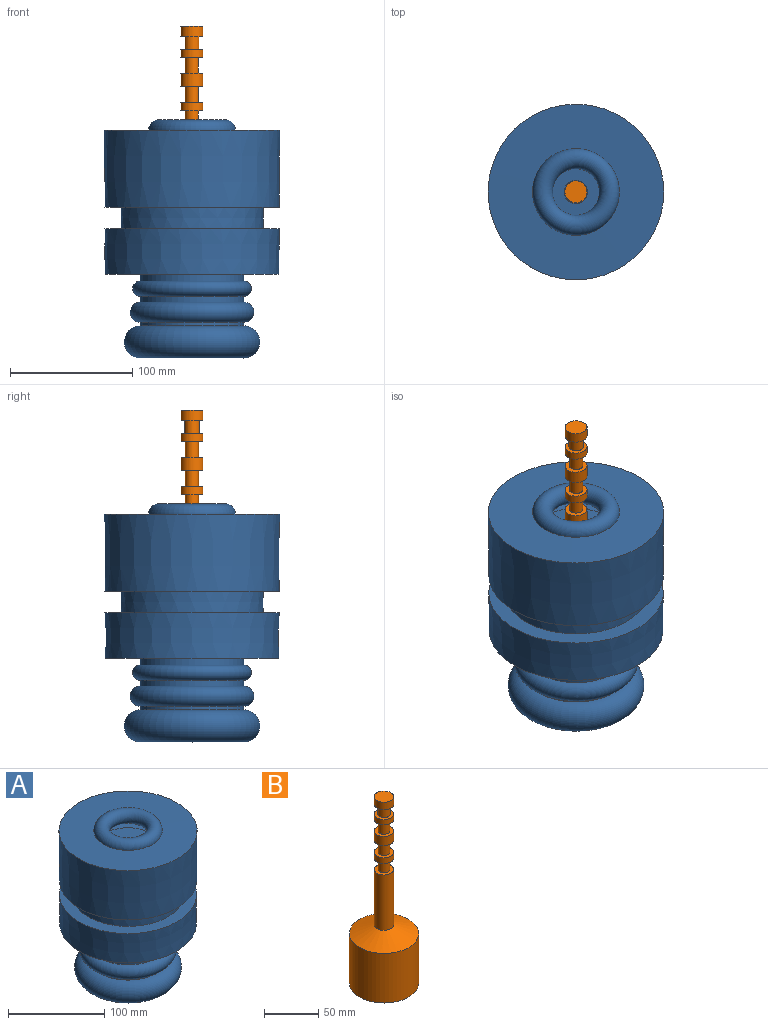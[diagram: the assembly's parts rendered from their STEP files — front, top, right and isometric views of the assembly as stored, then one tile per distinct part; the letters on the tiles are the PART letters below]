
ASSEMBLY  parts=2 mates=1
PART A: 47 faces, bbox 143.7x143.7x194.9 mm
  f0: torus R=42.43mm, axis (0,0,1), area 7727.4mm2, adj f1,f46
  f1: cylinder r=42.43mm len=84.86mm, axis (0,0,1), area 785.9mm2, adj f0,f2
  f2: torus R=42.43mm, axis (0,0,1), area 17605.2mm2, adj f1,f3
  f3: plane 58.56x58.56mm, normal (0,0,-1), area 2693.2mm2, adj f2
  f4: plane 42.43x42.43mm, normal (0,0,1), area 1413.9mm2, adj f5
  f5: cone r=21.7mm half-angle=19.1deg, axis (0,0,-1), area 198.9mm2, adj f4,f6
  f6: plane 47.27x47.27mm, normal (0,0,1), area 275.7mm2, adj f5,f7
  f7: cylinder r=23.63mm len=47.27mm, axis (0,0,1), area 293mm2, adj f6,f8
  f8: plane 47.27x47.27mm, normal (0,0,-1), area 181.2mm2, adj f7,f9
  f9: cone r=24.95mm half-angle=19.1deg, axis (0,0,-1), area 1168.6mm2, adj f8,f10
  f10: plane 53.77x53.77mm, normal (0,0,1), area 315.3mm2, adj f9,f11
  f11: cylinder r=26.88mm len=53.77mm, axis (0,0,1), area 333.3mm2, adj f10,f12
  f12: plane 53.77x53.77mm, normal (0,0,-1), area 206.8mm2, adj f11,f13
  f13: cone r=28.2mm half-angle=19.1deg, axis (0,0,-1), area 1329.2mm2, adj f12,f14
  f14: plane 60.27x60.27mm, normal (0,0,1), area 354.8mm2, adj f13,f15
  f15: cylinder r=30.14mm len=60.27mm, axis (0,0,1), area 373.6mm2, adj f14,f16
  f16: plane 60.27x60.27mm, normal (0,0,-1), area 232.4mm2, adj f15,f17
  f17: cone r=31.45mm half-angle=19.1deg, axis (0,0,-1), area 1489.8mm2, adj f16,f18
  f18: plane 66.78x66.78mm, normal (0,0,1), area 394.4mm2, adj f17,f19
  f19: cylinder r=33.39mm len=66.78mm, axis (0,0,1), area 413.9mm2, adj f18,f20
  f20: plane 66.78x66.78mm, normal (0,0,-1), area 258mm2, adj f19,f21
  f21: cone r=34.21mm half-angle=19.1deg, axis (0,0,-1), area 1325.3mm2, adj f20,f22
  f22: cylinder r=34.21mm len=132.81mm, axis (0,0,1), area 28550.7mm2, adj f21,f23
  f23: plane 68.43x68.43mm, normal (0,0,-1), area 3394mm2, adj f22,f24
  f24: cone r=9.57mm half-angle=0.4deg, axis (0,0,1), area 604.3mm2, adj f23,f25
  f25: cone r=34.21mm half-angle=89.6deg, axis (0,0,-1), area 3389.9mm2, adj f24,f26
  f26: cone r=34.21mm half-angle=87.6deg, axis (0,0,1), area 1979.5mm2, adj f25,f27
  f27: cylinder r=42.43mm len=87.09mm, axis (0,0,1), area 23217mm2, adj f26,f28
  f28: plane 123.37x123.37mm, normal (0,0,1), area 6298.4mm2, adj f27,f29
  f29: cylinder r=61.68mm len=123.37mm, axis (0,0,1), area 7414.3mm2, adj f28,f30
  f30: plane 123.37x123.37mm, normal (0,0,-1), area 3486.3mm2, adj f29,f31
  f31: cylinder r=51.92mm len=103.83mm, axis (0,0,1), area 10488.8mm2, adj f30,f32
  f32: plane 123.37x123.37mm, normal (0,0,1), area 3486.3mm2, adj f31,f33
  f33: cylinder r=61.68mm len=123.37mm, axis (0,0,1), area 18141.4mm2, adj f32,f34
  f34: plane 123.37x123.37mm, normal (0,0,-1), area 9610.9mm2, adj f33,f35
  f35: cylinder r=27.31mm len=54.62mm, axis (0,0,1), area 173.6mm2, adj f34,f36
  f36: torus R=27.31mm, axis (0,0,1), area 6235.6mm2, adj f35,f37
  f37: cone r=71.85mm half-angle=89.6deg, axis (0,0,-1), area 12252.1mm2, adj f36,f38
  f38: cone r=71.85mm half-angle=0.4deg, axis (0,0,1), area 28376.4mm2, adj f37,f39
  f39: cone r=71.41mm half-angle=89.6deg, axis (0,0,-1), area 5295.4mm2, adj f38,f40
  f40: cone r=58.43mm half-angle=0.4deg, axis (0,0,1), area 6454.7mm2, adj f39,f41
  f41: plane 142.82x142.82mm, normal (0,0,1), area 5340.1mm2, adj f40,f42
  f42: cone r=71.41mm half-angle=0.4deg, axis (0,0,1), area 16778.3mm2, adj f41,f43
  f43: plane 142.3x142.3mm, normal (0,0,-1), area 10248.7mm2, adj f42,f44
  f44: cylinder r=42.43mm len=84.86mm, axis (0,0,1), area 1464.6mm2, adj f43,f45
  f45: torus R=42.43mm, axis (0,0,1), area 5626mm2, adj f44,f46
  f46: cylinder r=42.43mm len=84.86mm, axis (0,0,1), area 1311.3mm2, adj f0,f45
PART B: 21 faces, bbox 63.9x63.9x210.8 mm
  f0: cone r=31.95mm half-angle=66.8deg, axis (0,0,-1), area 3211.8mm2, adj f1,f20
  f1: cylinder r=31.95mm len=63.89mm, axis (0,0,1), area 11248.6mm2, adj f0,f2
  f2: plane 63.89x63.89mm, normal (0,0,-1), area 3206mm2, adj f1
  f3: plane 17.99x17.99mm, normal (0,0,1), area 254.1mm2, adj f4
  f4: cylinder r=8.99mm len=17.99mm, axis (0,0,1), area 487.4mm2, adj f3,f5
  f5: plane 17.99x17.99mm, normal (0,0,-1), area 149mm2, adj f4,f6
  f6: cylinder r=5.78mm len=11.57mm, axis (0,0,1), area 399.4mm2, adj f5,f7
  f7: plane 17.99x17.99mm, normal (0,0,1), area 149mm2, adj f6,f8
  f8: cylinder r=8.99mm len=17.99mm, axis (0,0,1), area 345mm2, adj f7,f9
  f9: plane 17.99x17.99mm, normal (0,0,-1), area 163.3mm2, adj f8,f10
  f10: cylinder r=5.38mm len=13.02mm, axis (0,0,1), area 440.1mm2, adj f9,f11
  f11: plane 17.99x17.99mm, normal (0,0,1), area 163.3mm2, adj f10,f12
  f12: cylinder r=8.99mm len=17.99mm, axis (0,0,1), area 586.5mm2, adj f11,f13
  f13: plane 17.99x17.99mm, normal (0,0,-1), area 163.3mm2, adj f12,f14
  f14: cylinder r=5.38mm len=13.64mm, axis (0,0,1), area 460.7mm2, adj f13,f15
  f15: plane 17.99x17.99mm, normal (0,0,1), area 163.3mm2, adj f14,f16
  f16: cylinder r=8.99mm len=17.99mm, axis (0,0,1), area 379.5mm2, adj f15,f17
  f17: plane 17.99x17.99mm, normal (0,0,-1), area 163.3mm2, adj f16,f18
  f18: cylinder r=5.38mm len=12.82mm, axis (0,0,1), area 433.2mm2, adj f17,f19
  f19: plane 17.99x17.99mm, normal (0,0,1), area 163.3mm2, adj f18,f20
  f20: cylinder r=8.99mm len=62.63mm, axis (0,0,1), area 3539.5mm2, adj f0,f19
PLACE A t=(-149.44,-12.86,102.15)mm
PLACE B t=(-149.44,-12.86,73.66)mm
MATE slider B.f0 <-> A.f0  axis (0,0,-1) through (-149.44,-12.86,73.66)mm
